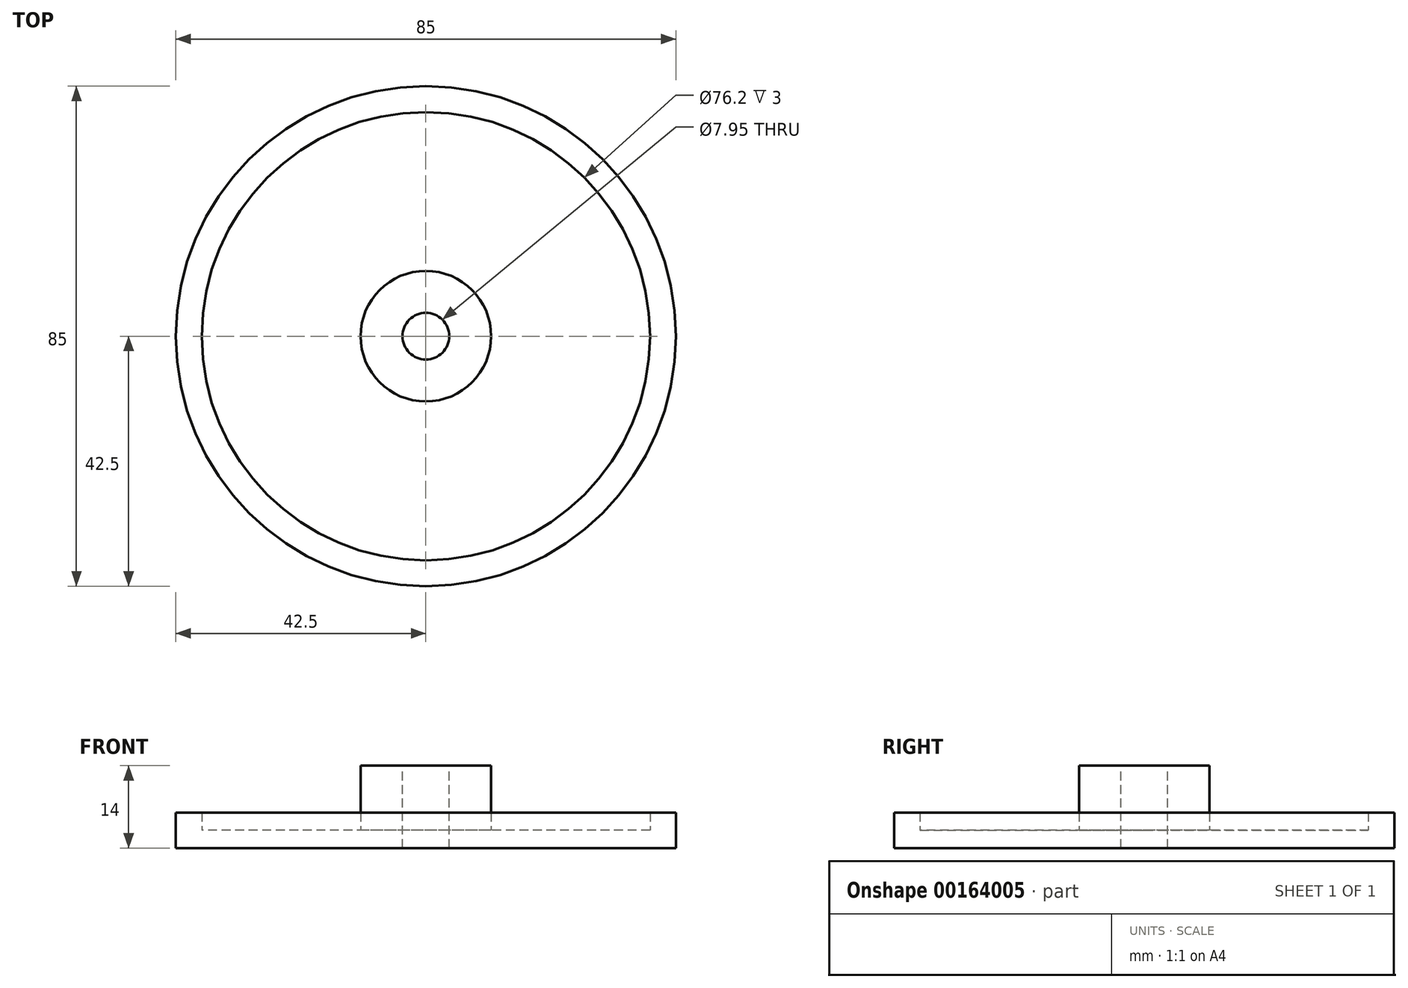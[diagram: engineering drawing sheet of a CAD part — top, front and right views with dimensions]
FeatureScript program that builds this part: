
annotation { "Feature Type Name" : "Feature", "Feature Type Description" : "" }
export const myFeature = defineFeature(function(context is Context, id is Id, definition is map)
    precondition{}
    {
        {
            var Q0;
            Q0=qCreatedBy(makeId("Top.planeOp"),FACE);
            var sketch = newSketch(context, id + "F0", { "sketchPlane" : qUnion([Q0])});
            skCircle(sketch, "E0", {"center": v(0, 0) * mm, "radius": 38.1 * mm});
            skCircle(sketch, "E1", {"center": v(0, 0) * mm, "radius": 42.5 * mm});
            skSolve(sketch);
        }
        {
            var Q0;
            Q0=makeQuery(id+"F0.imprint","IMPRINT",FACE,{"disambiguationData":[TD([[makeQuery(id+"F0.imprint","IMPRINT",EDGE,{"derivedFrom":sQuery(id+"F0.wireOp",EDGE,"E0")}),-1.0]])]});
            var sketch = newSketch(context, id + "F1", { "sketchPlane" : qUnion([Q0])});
            skSolve(sketch);
        }
        {
            var Q0;
            Q0 = qSketchRegion(id + "F0", true);
            extrude(context, id + "F2", {"entities" : qUnion([Q0]), "depth" : 6 * mm});
        }
        {
            var Q0;
            Q0=makeQuery(id+"F1.imprint","IMPRINT",FACE,{"disambiguationData":[TD([[makeQuery(id+"F1.imprint","IMPRINT",EDGE,{"derivedFrom":makeQuery(id+"F0.imprint","IMPRINT",EDGE,{"derivedFrom":sQuery(id+"F0.wireOp",EDGE,"E0")})}),1.0]])]});
            extrude(context, id + "F3", {"entities" : qUnion([Q0]), "operationType" : NewBodyOperationType.ADD, "depth" : 3 * mm});
        }
        {
            var Q0;
            Q0=makeQuery(id+"F3.opExtrude","CAP_FACE",FACE,{"disambiguationData":[OSD([sQuery(id+"F0.wireOp",EDGE,"E0")])],"isStart":false});
            var sketch = newSketch(context, id + "F4", { "sketchPlane" : qUnion([Q0])});
            skPoint(sketch, "E2", {"position": v(0, 0) * mm});
            skSolve(sketch);
        }
        {
            var Q0;
            Q0=sQuery(id+"F4.wireOp",VERTEX,"E2");
            var Q1;
            Q1=makeQuery(id+"F2.opExtrude","SWEPT_BODY",BODY,{"disambiguationData":[OSD([sQuery(id+"F0.wireOp",EDGE,"E0"),sQuery(id+"F0.wireOp",EDGE,"E1")])]});
            hole(context, id + "F5", {"style" : HoleStyle.SIMPLE, "endStyle" : HoleEndStyle.BLIND, "holeDiameter" : 7.95 * mm, "holeDepth" : 16 * mm, "startFromSketch" : true, "locations" : qUnion([Q0]), "scope" : qUnion([Q1])});
        }
        {
            var Q0;
            Q0=makeQuery(id+"F2.opExtrude","SWEPT_BODY",BODY,{"disambiguationData":[OSD([sQuery(id+"F0.wireOp",EDGE,"E0"),sQuery(id+"F0.wireOp",EDGE,"E1")])]});
            transform(context, id + "F6", {"entities" : qUnion([Q0]), "transformType" : TransformType.TRANSLATION_3D, "dx" : 0 * mm, "dy" : 0 * mm, "dz" : 0 * mm, "makeCopy" : true});
        }
        {
            var Q0;
            Q0=makeQuery(id+"F3.opExtrude","CAP_FACE",FACE,{"disambiguationData":[OSD([sQuery(id+"F0.wireOp",EDGE,"E0")])],"isStart":false});
            var sketch = newSketch(context, id + "F7", { "sketchPlane" : qUnion([Q0])});
            skCircle(sketch, "E3", {"center": v(0, 0) * mm, "radius": 11.1 * mm});
            skCircle(sketch, "E4", {"center": v(0, 0) * mm, "radius": 3.98 * mm});
            skSolve(sketch);
        }
        {
            var Q0;
            Q0=makeQuery(id+"F7.imprint","IMPRINT",FACE,{"disambiguationData":[TD([[makeQuery(id+"F7.imprint","IMPRINT",EDGE,{"derivedFrom":sQuery(id+"F7.wireOp",EDGE,"E3")}),1.0]])]});
            extrude(context, id + "F8", {"entities" : qUnion([Q0]), "operationType" : NewBodyOperationType.ADD, "depth" : 11 * mm});
        }
    });
